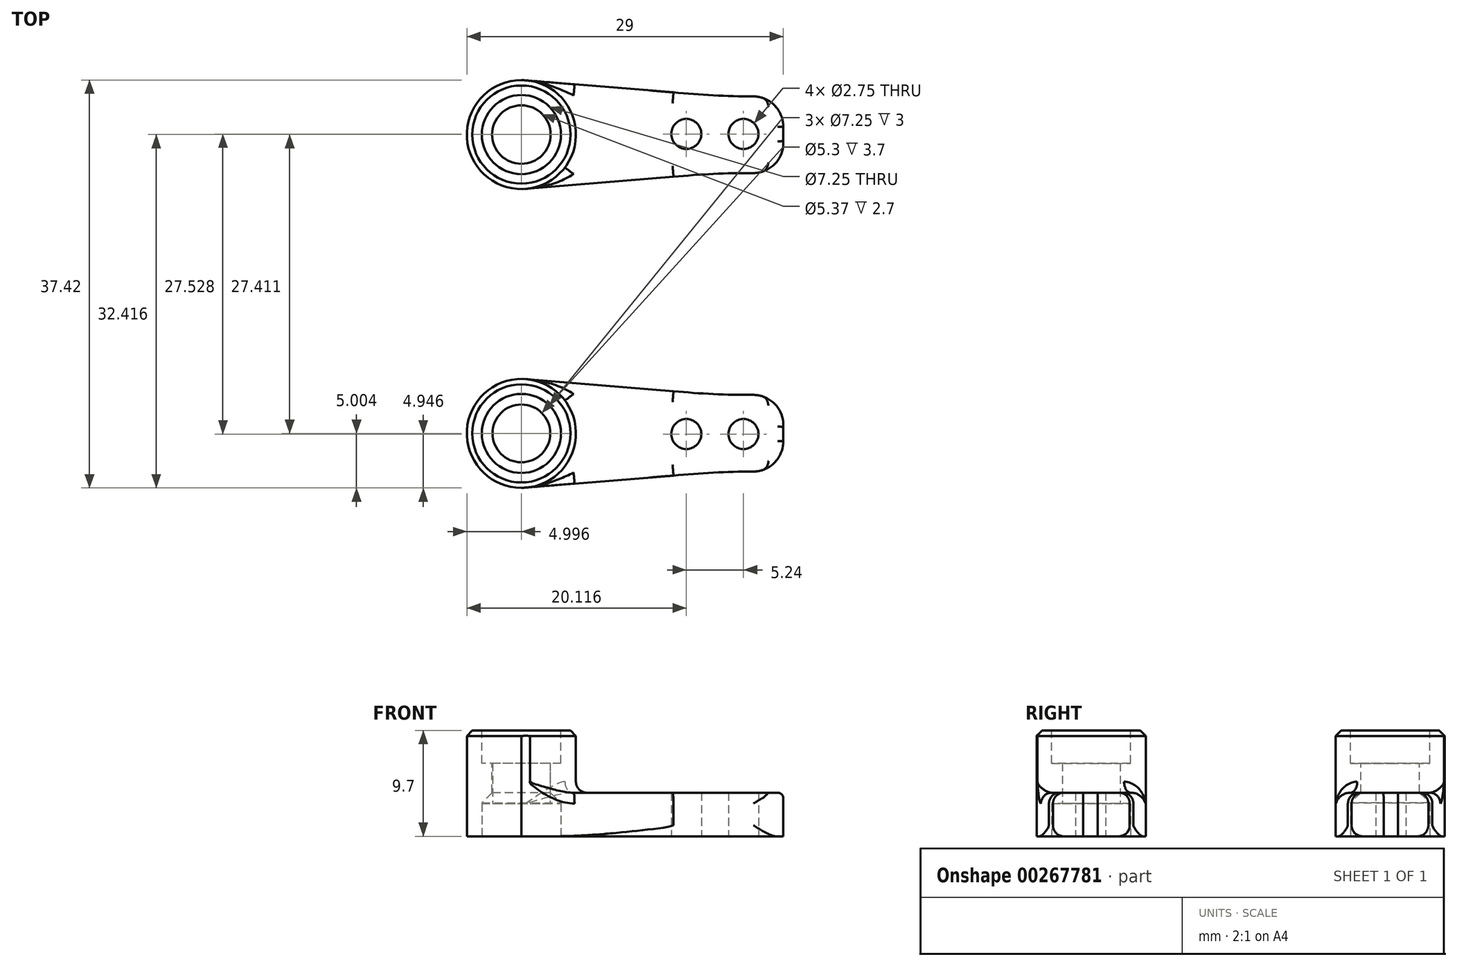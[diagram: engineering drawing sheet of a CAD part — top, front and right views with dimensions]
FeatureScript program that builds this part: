
annotation { "Feature Type Name" : "Feature", "Feature Type Description" : "" }
export const myFeature = defineFeature(function(context is Context, id is Id, definition is map)
    precondition{}
    {
        {
            var Q0;
            Q0=qCreatedBy(makeId("Top.planeOp"),FACE);
            var sketch = newSketch(context, id + "F0", { "sketchPlane" : qUnion([Q0])});
            skArc(sketch, "E0", {"start": v(-24.45, 18.7) * mm, "mid": v(-24.86, 8.72) * mm, "end": v(-23.65, 18.64) * mm});
            skLineSegment(sketch, "E1", {"start": v(-24.45, 18.7) * mm, "end": v(-10.5, 17.58) * mm});
            skLineSegment(sketch, "E2", {"start": v(-10.5, 9.83) * mm, "end": v(-24.05, 8.72) * mm});
            skPoint(sketch, "E3.orphan", {"position": v(-5.94, 13.7) * mm});
            skPoint(sketch, "E4.orphan", {"position": v(-24.45, 8.69) * mm});
            skLineSegment(sketch, "E5.left", {"start": v(-5.94, 10.2) * mm, "end": v(-5.94, 10.17) * mm});
            skLineSegment(sketch, "E5.right", {"start": v(-0.45, 14.5) * mm, "end": v(-0.45, 12.74) * mm});
            skArc(sketch, "E6", {"start": v(-3.2, 10.17) * mm, "mid": v(-6.86, 10.1) * mm, "end": v(-10.5, 9.83) * mm});
            skArc(sketch, "E7", {"start": v(-10.5, 17.58) * mm, "mid": v(-6.86, 17.3) * mm, "end": v(-3.2, 17.2) * mm});
            skPoint(sketch, "E8.orphan", {"position": v(-5.94, 17.2) * mm});
            skArc(sketch, "E9", {"start": v(-0.45, 14.42) * mm, "mid": v(-1.24, 16.39) * mm, "end": v(-3.2, 17.2) * mm});
            skArc(sketch, "E10", {"start": v(-3.2, 10.17) * mm, "mid": v(-1.19, 11.04) * mm, "end": v(-0.45, 13.1) * mm});
            skPoint(sketch, "E5.bottom.end.orphan", {"position": v(-0.45, 17.2) * mm});
            skPoint(sketch, "E5.top.end.orphan", {"position": v(-0.45, 10.17) * mm});
            skSolve(sketch);
        }
        {
            var Q0;
            {var subQ0=sQuery(id+"F0.wireOp",EDGE,"E1");var subQ1=sQuery(id+"F0.wireOp",EDGE,"E0");var subQ2=makeQuery(id+"F0.imprint","INTERSECT",VERTEX,{"disambiguationData":[OD(0.0)],"derivedFrom":[subQ1,subQ0]});Q0=makeQuery(id+"F0.imprint","IMPRINT",FACE,{"disambiguationData":[TD([[makeQuery(id+"F0.imprint","IMPRINT",EDGE,{"disambiguationData":[TD([[subQ2,-1.0]])],"derivedFrom":subQ1}),1.0]])]});}
            extrude(context, id + "F1", {"entities" : qUnion([Q0]), "depth" : 9.7 * mm});
        }
        {
            var Q0;
            Q0 = qSketchRegion(id + "F0", true);
            extrude(context, id + "F2", {"entities" : qUnion([Q0]), "operationType" : NewBodyOperationType.ADD, "depth" : 4 * mm});
        }
        {
            var Q0;
            Q0=makeQuery(id+"F1.opExtrude","CAP_FACE",FACE,{"disambiguationData":[OSD([sQuery(id+"F0.wireOp",EDGE,"E0"),sQuery(id+"F0.wireOp",EDGE,"E1")])],"isStart":false});
            var sketch = newSketch(context, id + "F3", { "sketchPlane" : qUnion([Q0])});
            skCircle(sketch, "E11", {"center": v(-24.45, 13.7) * mm, "radius": 3.62 * mm});
            skSolve(sketch);
        }
        {
            var Q0;
            Q0 = qSketchRegion(id + "F3", true);
            extrude(context, id + "F4", {"entities" : qUnion([Q0]), "operationType" : NewBodyOperationType.REMOVE, "oppositeDirection" : true, "depth" : 3 * mm});
        }
        {
            var Q0;
            Q0=makeQuery(id+"F4.boolean.opBoolean","COPY",FACE,{"derivedFrom":makeQuery(id+"F4.opExtrude","CAP_FACE",FACE,{"disambiguationData":[OSD([sQuery(id+"F3.wireOp",EDGE,"E11")])],"isStart":false})});
            var sketch = newSketch(context, id + "F5", { "sketchPlane" : qUnion([Q0])});
            skCircle(sketch, "E12", {"center": v(-24.45, 13.7) * mm, "radius": 1.75 * mm});
            skSolve(sketch);
        }
        {
            var Q0;
            Q0 = qSketchRegion(id + "F5", true);
            extrude(context, id + "F6", {"entities" : qUnion([Q0]), "operationType" : NewBodyOperationType.REMOVE, "oppositeDirection" : true, "depth" : 25 * mm});
        }
        {
            var Q0;
            {var subQ0=sQuery(id+"F0.wireOp",EDGE,"E1");var subQ1=sQuery(id+"F0.wireOp",EDGE,"E0");Q0=makeQuery(id+"F2.boolean.opBoolean","MERGE",FACE,{"derivedFrom":[makeQuery(id+"F1.opExtrude","CAP_FACE",FACE,{"disambiguationData":[OSD([subQ1,subQ0])],"isStart":true}),makeQuery(id+"F2.opExtrude","CAP_FACE",FACE,{"disambiguationData":[OSD([subQ1,subQ0,sQuery(id+"F0.wireOp",EDGE,"E2"),sQuery(id+"F0.wireOp",EDGE,"E5.right"),sQuery(id+"F0.wireOp",EDGE,"E6"),sQuery(id+"F0.wireOp",EDGE,"E7"),sQuery(id+"F0.wireOp",EDGE,"E9"),sQuery(id+"F0.wireOp",EDGE,"E10")])],"isStart":true})]});}
            var sketch = newSketch(context, id + "F7", { "sketchPlane" : qUnion([Q0])});
            skCircle(sketch, "E13", {"center": v(-24.45, -13.7) * mm, "radius": 3.62 * mm});
            skSolve(sketch);
        }
        {
            var Q0;
            Q0 = qSketchRegion(id + "F7", true);
            extrude(context, id + "F8", {"entities" : qUnion([Q0]), "operationType" : NewBodyOperationType.REMOVE, "oppositeDirection" : true, "depth" : 3 * mm});
        }
        {
            var Q0;
            {var subQ0=sQuery(id+"F0.wireOp",EDGE,"E1");var subQ1=sQuery(id+"F0.wireOp",EDGE,"E0");Q0=makeQuery(id+"F2.boolean.opBoolean","MERGE",FACE,{"derivedFrom":[makeQuery(id+"F1.opExtrude","CAP_FACE",FACE,{"disambiguationData":[OSD([subQ1,subQ0])],"isStart":true}),makeQuery(id+"F2.opExtrude","CAP_FACE",FACE,{"disambiguationData":[OSD([subQ1,subQ0,sQuery(id+"F0.wireOp",EDGE,"E2"),sQuery(id+"F0.wireOp",EDGE,"E5.right"),sQuery(id+"F0.wireOp",EDGE,"E6"),sQuery(id+"F0.wireOp",EDGE,"E7"),sQuery(id+"F0.wireOp",EDGE,"E9"),sQuery(id+"F0.wireOp",EDGE,"E10")])],"isStart":true})]});}
            var sketch = newSketch(context, id + "F9", { "sketchPlane" : qUnion([Q0])});
            skCircle(sketch, "E14", {"center": v(-4.1, -13.76) * mm, "radius": 1.38 * mm});
            skPoint(sketch, "E15.start.orphan", {"position": v(-0.45, -13.76) * mm});
            skCircle(sketch, "E16", {"center": v(-9.33, -13.76) * mm, "radius": 1.38 * mm});
            skSolve(sketch);
        }
        {
            var Q0;
            Q0 = qSketchRegion(id + "F9", true);
            extrude(context, id + "F10", {"entities" : qUnion([Q0]), "operationType" : NewBodyOperationType.REMOVE, "oppositeDirection" : true, "depth" : 25 * mm});
        }
        {
            var Q0;
            Q0=makeQuery(id+"F2.opExtrude","CAP_FACE",FACE,{"disambiguationData":[OSD([sQuery(id+"F0.wireOp",EDGE,"E0"),sQuery(id+"F0.wireOp",EDGE,"E1"),sQuery(id+"F0.wireOp",EDGE,"E2"),sQuery(id+"F0.wireOp",EDGE,"E5.right"),sQuery(id+"F0.wireOp",EDGE,"E6"),sQuery(id+"F0.wireOp",EDGE,"E7"),sQuery(id+"F0.wireOp",EDGE,"E9"),sQuery(id+"F0.wireOp",EDGE,"E10")])],"isStart":false});
            var sketch = newSketch(context, id + "F11", { "sketchPlane" : qUnion([Q0])});
            skSolve(sketch);
        }
        {
            var Q0;
            {var subQ0=sQuery(id+"F0.wireOp",EDGE,"E0");Q0=makeQuery(id+"F2.boolean.opBoolean","INTERSECT",EDGE,{"derivedFrom":[makeQuery(id+"F1.opExtrude","SWEPT_FACE",FACE,{"disambiguationData":[OSD([subQ0])]}),makeQuery(id+"F2.opExtrude","CAP_FACE",FACE,{"disambiguationData":[OSD([subQ0,sQuery(id+"F0.wireOp",EDGE,"E1"),sQuery(id+"F0.wireOp",EDGE,"E2"),sQuery(id+"F0.wireOp",EDGE,"E5.right"),sQuery(id+"F0.wireOp",EDGE,"E6"),sQuery(id+"F0.wireOp",EDGE,"E7"),sQuery(id+"F0.wireOp",EDGE,"E9"),sQuery(id+"F0.wireOp",EDGE,"E10")])],"isStart":false})]});}
            var Q1;
            Q1=makeQuery(id+"F2.opExtrude","CAP_EDGE",EDGE,{"disambiguationData":[OSD([sQuery(id+"F0.wireOp",EDGE,"E2")])],"isStart":false});
            var Q2;
            Q2=makeQuery(id+"F2.opExtrude","CAP_EDGE",EDGE,{"disambiguationData":[OSD([sQuery(id+"F0.wireOp",EDGE,"E1")])],"isStart":false});
            var Q3;
            Q3=makeQuery(id+"F2.opExtrude","CAP_EDGE",EDGE,{"disambiguationData":[OSD([sQuery(id+"F0.wireOp",EDGE,"E6")])],"isStart":true});
            var Q4;
            Q4=makeQuery(id+"F2.opExtrude","CAP_EDGE",EDGE,{"disambiguationData":[OSD([sQuery(id+"F0.wireOp",EDGE,"E7")])],"isStart":true});
            fillet(context, id + "F12", {"entities" : qUnion([Q0, Q1, Q2, Q3, Q4]), "radius" : 1 * mm, "tangentPropagation" : true, "allowEdgeOverflow" : false});
        }
        {
            var Q0;
            Q0=makeQuery(id+"F2.opExtrude","CAP_EDGE",EDGE,{"disambiguationData":[OSD([sQuery(id+"F0.wireOp",EDGE,"E5.right")])],"isStart":false});
            fillet(context, id + "F13", {"entities" : qUnion([Q0]), "radius" : 0.5 * mm, "tangentPropagation" : true, "allowEdgeOverflow" : false});
        }
        {
            var Q0;
            Q0=makeQuery(id+"F1.opExtrude","SWEPT_BODY",BODY,{"disambiguationData":[OSD([sQuery(id+"F0.wireOp",EDGE,"E0"),sQuery(id+"F0.wireOp",EDGE,"E1")])]});
            var Q1;
            Q1=qCreatedBy(makeId("Front.planeOp"),FACE);
            mirror(context, id + "F14", {"operationType" : NewBodyOperationType.ADD, "entities" : qUnion([Q0]), "mirrorPlane" : qUnion([Q1])});
        }
        {
            var Q0;
            Q0=makeQuery(id+"F14.opPattern","COPY",FACE,{"derivedFrom":makeQuery(id+"F8.boolean.opBoolean","COPY",FACE,{"derivedFrom":makeQuery(id+"F8.opExtrude","CAP_FACE",FACE,{"disambiguationData":[OSD([sQuery(id+"F7.wireOp",EDGE,"E13")])],"isStart":false})}),"instanceName":"1"});
            var sketch = newSketch(context, id + "F15", { "sketchPlane" : qUnion([Q0])});
            skCircle(sketch, "E17", {"center": v(-24.45, 13.7) * mm, "radius": 2.65 * mm});
            skSolve(sketch);
        }
        {
            var Q0;
            Q0 = qSketchRegion(id + "F15", true);
            extrude(context, id + "F16", {"entities" : qUnion([Q0]), "operationType" : NewBodyOperationType.REMOVE, "oppositeDirection" : true, "depth" : 25 * mm});
        }
        {
            var Q0;
            Q0=makeQuery(id+"F4.boolean.opBoolean","COPY",FACE,{"derivedFrom":makeQuery(id+"F4.opExtrude","CAP_FACE",FACE,{"disambiguationData":[OSD([sQuery(id+"F3.wireOp",EDGE,"E11")])],"isStart":false})});
            var sketch = newSketch(context, id + "F17", { "sketchPlane" : qUnion([Q0])});
            skCircle(sketch, "E18", {"center": v(-24.45, 13.7) * mm, "radius": 2.68 * mm});
            skSolve(sketch);
        }
        {
            var Q0;
            Q0 = qSketchRegion(id + "F17", true);
            extrude(context, id + "F18", {"entities" : qUnion([Q0]), "operationType" : NewBodyOperationType.REMOVE, "oppositeDirection" : true, "depth" : 25 * mm});
        }
        {
            var Q0;
            Q0=makeQuery(id+"F16.boolean.opBoolean","COPY",EDGE,{"derivedFrom":makeQuery(id+"F16.opExtrude","CAP_EDGE",EDGE,{"disambiguationData":[OSD([sQuery(id+"F15.wireOp",EDGE,"E17")])],"isStart":true})});
            var Q1;
            Q1=makeQuery(id+"F18.boolean.opBoolean","INTERSECT",EDGE,{"derivedFrom":[makeQuery(id+"F8.boolean.opBoolean","COPY",FACE,{"derivedFrom":makeQuery(id+"F8.opExtrude","CAP_FACE",FACE,{"disambiguationData":[OSD([sQuery(id+"F7.wireOp",EDGE,"E13")])],"isStart":false})}),makeQuery(id+"F18.opExtrude","SWEPT_FACE",FACE,{"disambiguationData":[OSD([sQuery(id+"F17.wireOp",EDGE,"E18")])]})]});
            chamfer(context, id + "F19", {"entities" : qUnion([Q0, Q1]), "width" : 1 * mm});
        }
        {
            var Q0;
            Q0=makeQuery(id+"F1.opExtrude","CAP_EDGE",EDGE,{"disambiguationData":[OSD([sQuery(id+"F0.wireOp",EDGE,"E0")])],"isStart":false});
            var Q1;
            Q1=makeQuery(id+"F4.boolean.opBoolean","COPY",EDGE,{"derivedFrom":makeQuery(id+"F4.opExtrude","CAP_EDGE",EDGE,{"disambiguationData":[OSD([sQuery(id+"F3.wireOp",EDGE,"E11")])],"isStart":true})});
            var Q2;
            Q2=makeQuery(id+"F14.opPattern","COPY",EDGE,{"derivedFrom":makeQuery(id+"F1.opExtrude","CAP_EDGE",EDGE,{"disambiguationData":[OSD([sQuery(id+"F0.wireOp",EDGE,"E0")])],"isStart":false}),"instanceName":"1"});
            var Q3;
            Q3=makeQuery(id+"F14.opPattern","COPY",EDGE,{"derivedFrom":makeQuery(id+"F4.boolean.opBoolean","COPY",EDGE,{"derivedFrom":makeQuery(id+"F4.opExtrude","CAP_EDGE",EDGE,{"disambiguationData":[OSD([sQuery(id+"F3.wireOp",EDGE,"E11")])],"isStart":true})}),"instanceName":"1"});
            chamfer(context, id + "F20", {"entities" : qUnion([Q0, Q1, Q2, Q3]), "width" : .5 * mm, "tangentPropagation" : true});
        }
    });
